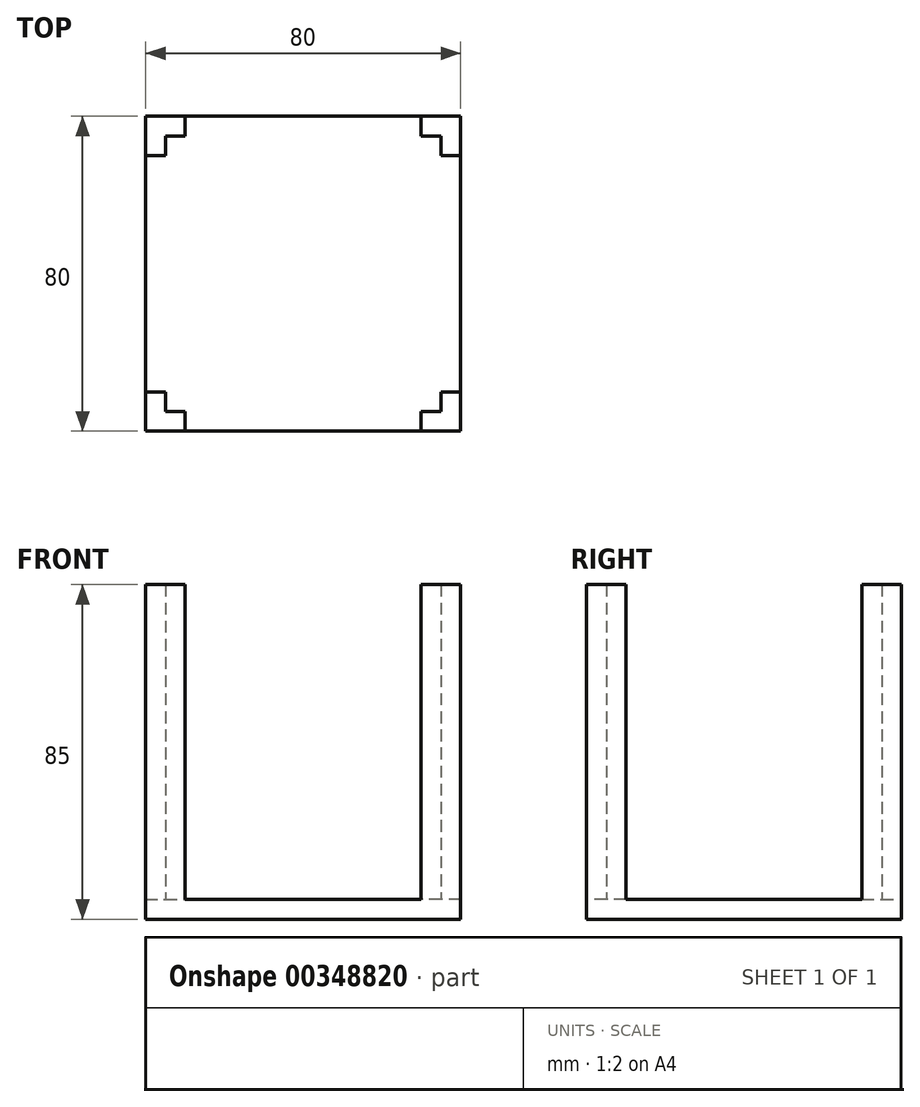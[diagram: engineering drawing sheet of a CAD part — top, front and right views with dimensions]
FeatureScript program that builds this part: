
annotation { "Feature Type Name" : "Feature", "Feature Type Description" : "" }
export const myFeature = defineFeature(function(context is Context, id is Id, definition is map)
    precondition{}
    {
        {
            var Q0;
            Q0=qCreatedBy(makeId("Top.planeOp"),FACE);
            var sketch = newSketch(context, id + "F0", { "sketchPlane" : qUnion([Q0])});
            skLineSegment(sketch, "E0.bottom", {"start": v(-40, 40) * mm, "end": v(40, 40) * mm});
            skLineSegment(sketch, "E0.top", {"start": v(-40, -40) * mm, "end": v(40, -40) * mm});
            skLineSegment(sketch, "E0.left", {"start": v(-40, 40) * mm, "end": v(-40, -40) * mm});
            skLineSegment(sketch, "E0.right", {"start": v(40, 40) * mm, "end": v(40, -40) * mm});
            skSolve(sketch);
        }
        {
            var Q0;
            Q0=makeQuery(id+"F0.imprint","IMPRINT",FACE,{"disambiguationData":[TD([[makeQuery(id+"F0.imprint","IMPRINT",EDGE,{"derivedFrom":sQuery(id+"F0.wireOp",EDGE,"E0.bottom")}),-1.0]])]});
            extrude(context, id + "F1", {"entities" : qUnion([Q0]), "depth" : 5 * mm});
        }
        {
            var Q0;
            Q0=makeQuery(id+"F1.opExtrude","CAP_FACE",FACE,{"disambiguationData":[OSD([sQuery(id+"F0.wireOp",EDGE,"E0.bottom"),sQuery(id+"F0.wireOp",EDGE,"E0.top"),sQuery(id+"F0.wireOp",EDGE,"E0.left"),sQuery(id+"F0.wireOp",EDGE,"E0.right")])],"isStart":false});
            var sketch = newSketch(context, id + "F2", { "sketchPlane" : qUnion([Q0])});
            skLineSegment(sketch, "E1", {"start": v(30, 40) * mm, "end": v(40, 40) * mm});
            skLineSegment(sketch, "E2", {"start": v(40, 40) * mm, "end": v(40, 30) * mm});
            skLineSegment(sketch, "E3", {"start": v(40, 30) * mm, "end": v(35, 30) * mm});
            skLineSegment(sketch, "E4", {"start": v(35, 30) * mm, "end": v(35, 35) * mm});
            skLineSegment(sketch, "E5", {"start": v(35, 35) * mm, "end": v(30, 35) * mm});
            skLineSegment(sketch, "E6", {"start": v(30, 35) * mm, "end": v(30, 40) * mm});
            skLineSegment(sketch, "E7.MirrorCS", {"start": v(35, -30) * mm, "end": v(35, -35) * mm});
            skLineSegment(sketch, "E8.MirrorCS", {"start": v(30, -40) * mm, "end": v(40, -40) * mm});
            skLineSegment(sketch, "E9.MirrorCS", {"start": v(30, -35) * mm, "end": v(30, -40) * mm});
            skLineSegment(sketch, "E10.MirrorCS", {"start": v(35, -35) * mm, "end": v(30, -35) * mm});
            skLineSegment(sketch, "E11.MirrorCS", {"start": v(40, -40) * mm, "end": v(40, -30) * mm});
            skLineSegment(sketch, "E12.MirrorCS", {"start": v(40, -30) * mm, "end": v(35, -30) * mm});
            skLineSegment(sketch, "E13.MirrorCS", {"start": v(-30, -35) * mm, "end": v(-30, -40) * mm});
            skLineSegment(sketch, "E14.MirrorCS", {"start": v(-35, -35) * mm, "end": v(-30, -35) * mm});
            skLineSegment(sketch, "E15.MirrorCS", {"start": v(-35, 30) * mm, "end": v(-35, 35) * mm});
            skLineSegment(sketch, "E16.MirrorCS", {"start": v(-40, -30) * mm, "end": v(-35, -30) * mm});
            skLineSegment(sketch, "E17.MirrorCS", {"start": v(-35, 35) * mm, "end": v(-30, 35) * mm});
            skLineSegment(sketch, "E18.MirrorCS", {"start": v(-35, -30) * mm, "end": v(-35, -35) * mm});
            skLineSegment(sketch, "E19.MirrorCS", {"start": v(-30, 35) * mm, "end": v(-30, 40) * mm});
            skLineSegment(sketch, "E20.MirrorCS", {"start": v(-40, 30) * mm, "end": v(-35, 30) * mm});
            skLineSegment(sketch, "E21.MirrorCS", {"start": v(-30, -40) * mm, "end": v(-40, -40) * mm});
            skLineSegment(sketch, "E22.MirrorCS", {"start": v(-40, 40) * mm, "end": v(-40, 30) * mm});
            skLineSegment(sketch, "E23.MirrorCS", {"start": v(-30, 40) * mm, "end": v(-40, 40) * mm});
            skLineSegment(sketch, "E24.MirrorCS", {"start": v(-40, -40) * mm, "end": v(-40, -30) * mm});
            skSolve(sketch);
        }
        {
            var Q0;
            Q0 = qSketchRegion(id + "F2", true);
            extrude(context, id + "F3", {"entities" : qUnion([Q0]), "operationType" : NewBodyOperationType.ADD, "depth" : 80 * mm});
        }
    });
